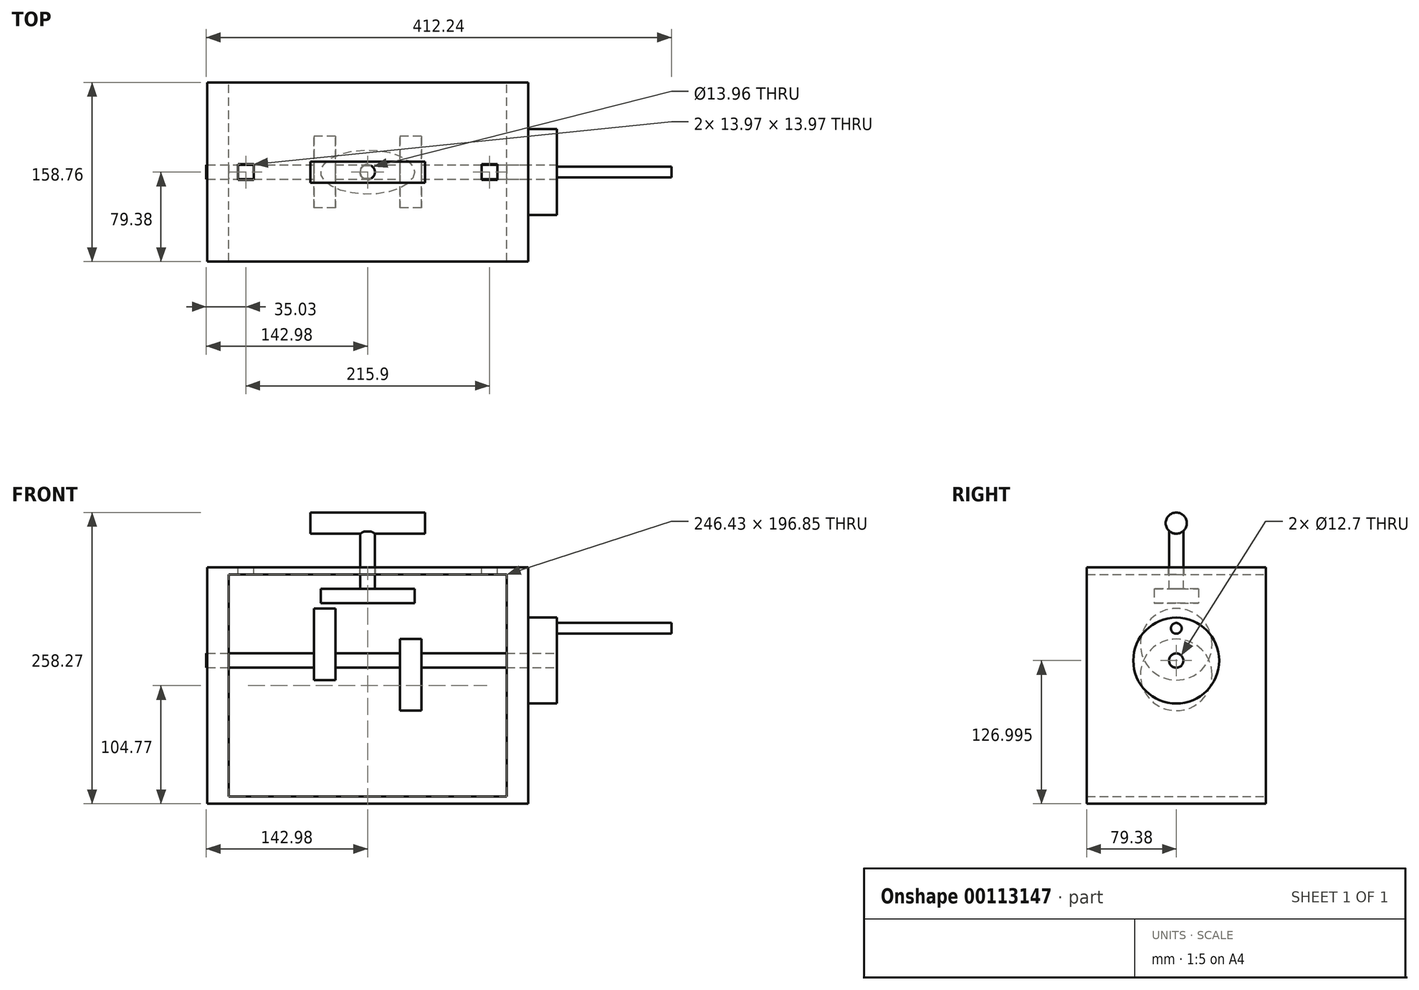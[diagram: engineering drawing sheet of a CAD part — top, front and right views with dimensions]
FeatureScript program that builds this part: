
annotation { "Feature Type Name" : "Feature", "Feature Type Description" : "" }
export const myFeature = defineFeature(function(context is Context, id is Id, definition is map)
    precondition{}
    {
        {
            var Q0;
            Q0=qCreatedBy(makeId("Front.planeOp"),FACE);
            var sketch = newSketch(context, id + "F0", { "sketchPlane" : qUnion([Q0])});
            skLineSegment(sketch, "E0.bottom", {"start": v(142.26, 104.78) * mm, "end": v(-142.26, 104.77) * mm});
            skLineSegment(sketch, "E0.top", {"start": v(142.26, -104.77) * mm, "end": v(-142.26, -104.78) * mm});
            skLineSegment(sketch, "E0.left", {"start": v(142.26, 104.78) * mm, "end": v(142.26, -104.77) * mm});
            skLineSegment(sketch, "E0.right", {"start": v(-142.26, 104.77) * mm, "end": v(-142.26, -104.78) * mm});
            skPoint(sketch, "E0.middle", {"position": v(0, 0) * mm});
            skLineSegment(sketch, "E1.bottom", {"start": v(123.21, 98.43) * mm, "end": v(-123.21, 98.42) * mm});
            skLineSegment(sketch, "E1.top", {"start": v(123.21, -98.43) * mm, "end": v(-123.21, -98.43) * mm});
            skLineSegment(sketch, "E1.left", {"start": v(123.21, 98.43) * mm, "end": v(123.21, -98.42) * mm});
            skLineSegment(sketch, "E1.right", {"start": v(-123.21, 98.42) * mm, "end": v(-123.21, -98.43) * mm});
            skSolve(sketch);
        }
        {
            var Q0;
            Q0 = qSketchRegion(id + "F0", true);
            extrude(context, id + "F1", {"entities" : qUnion([Q0]), "endBound" : BoundingType.SYMMETRIC, "depth" : 158.75 * mm});
        }
        {
            var Q0;
            Q0=makeQuery(id+"F1.opExtrude","SWEPT_FACE",FACE,{"disambiguationData":[OSD([sQuery(id+"F0.wireOp",EDGE,"E0.left")])]});
            var sketch = newSketch(context, id + "F2", { "sketchPlane" : qUnion([Q0])});
            skCircle(sketch, "E2", {"center": v(0, 22.22) * mm, "radius": 38.1 * mm});
            skSolve(sketch);
        }
        {
            var Q0;
            Q0=makeQuery(id+"F2.imprint","IMPRINT",FACE,{"disambiguationData":[TD([[makeQuery(id+"F2.imprint","IMPRINT",EDGE,{"derivedFrom":sQuery(id+"F2.wireOp",EDGE,"E2")}),1.0]])]});
            extrude(context, id + "F3", {"entities" : qUnion([Q0]), "depth" : 25.4 * mm});
        }
        {
            var Q0;
            Q0=makeQuery(id+"F3.opExtrude","CAP_FACE",FACE,{"disambiguationData":[OSD([sQuery(id+"F2.wireOp",EDGE,"E2")])],"isStart":false});
            var sketch = newSketch(context, id + "F4", { "sketchPlane" : qUnion([Q0])});
            skCircle(sketch, "E3", {"center": v(0, 50.8) * mm, "radius": 4.76 * mm});
            skLineSegment(sketch, "E4", {"start": v(0, 22.22) * mm, "end": v(0, 50.8) * mm, "construction": true});
            skSolve(sketch);
        }
        {
            var Q0;
            Q0 = qSketchRegion(id + "F4", true);
            extrude(context, id + "F5", {"entities" : qUnion([Q0]), "depth" : 101.6 * mm});
        }
        {
            var Q0;
            Q0=makeQuery(id+"F1.opExtrude","SWEPT_FACE",FACE,{"disambiguationData":[OSD([sQuery(id+"F0.wireOp",EDGE,"E0.left")])]});
            var sketch = newSketch(context, id + "F6", { "sketchPlane" : qUnion([Q0])});
            skCircle(sketch, "E5.0", {"center": v(0, 22.22) * mm, "radius": 38.1 * mm, "construction": true});
            skCircle(sketch, "E6", {"center": v(0, 22.22) * mm, "radius": 6.35 * mm});
            skSolve(sketch);
        }
        {
            var Q0;
            Q0 = qSketchRegion(id + "F6", true);
            extrude(context, id + "F7", {"entities" : qUnion([Q0]), "operationType" : NewBodyOperationType.REMOVE, "endBound" : BoundingType.THROUGH_ALL, "oppositeDirection" : true, "depth" : 25.4 * mm});
        }
        {
            var Q0;
            Q0=makeQuery(id+"F3.opExtrude","CAP_FACE",FACE,{"disambiguationData":[OSD([sQuery(id+"F2.wireOp",EDGE,"E2")])],"isStart":false});
            var sketch = newSketch(context, id + "F8", { "sketchPlane" : qUnion([Q0])});
            skCircle(sketch, "E7.0", {"center": v(0, 22.22) * mm, "radius": 6.35 * mm});
            skSolve(sketch);
        }
        {
            var Q0;
            Q0 = qSketchRegion(id + "F8", true);
            extrude(context, id + "F9", {"entities" : qUnion([Q0]), "oppositeDirection" : true, "depth" : 310.64 * mm});
        }
        {
            var Q0;
            Q0=makeQuery(id+"F1.opExtrude","SWEPT_FACE",FACE,{"disambiguationData":[OSD([sQuery(id+"F0.wireOp",EDGE,"E0.bottom")])]});
            var sketch = newSketch(context, id + "F10", { "sketchPlane" : qUnion([Q0])});
            skCircle(sketch, "E8", {"center": v(0, 0) * mm, "radius": 6.98 * mm});
            skSolve(sketch);
        }
        {
            var Q0;
            Q0 = qSketchRegion(id + "F10", true);
            extrude(context, id + "F11", {"entities" : qUnion([Q0]), "operationType" : NewBodyOperationType.REMOVE, "oppositeDirection" : true, "depth" : 25.4 * mm});
        }
        {
            var Q0;
            Q0=qCreatedBy(makeId("Right.planeOp"),FACE);
            cPlane(context, id + "F12", {"entities" : qUnion([Q0]), "cplaneType" : CPlaneType.OFFSET, "offset" : 38.1 * mm, "width" : 152.4 * mm, "height" : 152.4 * mm});
        }
        {
            var Q0;
            Q0=qCreatedBy(makeId("Right.planeOp"),FACE);
            cPlane(context, id + "F13", {"entities" : qUnion([Q0]), "cplaneType" : CPlaneType.OFFSET, "offset" : 38.1 * mm, "oppositeDirection" : true, "width" : 152.4 * mm, "height" : 152.4 * mm});
        }
        {
            var Q0;
            Q0=makeQuery(id+"F1.opExtrude","SWEPT_FACE",FACE,{"disambiguationData":[OSD([sQuery(id+"F0.wireOp",EDGE,"E0.bottom")])]});
            var sketch = newSketch(context, id + "F14", { "sketchPlane" : qUnion([Q0])});
            skCircle(sketch, "E9", {"center": v(0, 0) * mm, "radius": 6.45 * mm});
            skSolve(sketch);
        }
        {
            var Q0;
            Q0 = qSketchRegion(id + "F14", true);
            extrude(context, id + "F15", {"entities" : qUnion([Q0]), "endBound" : BoundingType.SYMMETRIC, "oppositeDirection" : true, "depth" : 63.5 * mm});
        }
        {
            var Q0;
            Q0=makeQuery(id+"F15.opExtrude","CAP_FACE",FACE,{"disambiguationData":[OSD([sQuery(id+"F14.wireOp",EDGE,"E9")])],"isStart":false});
            var sketch = newSketch(context, id + "F16", { "sketchPlane" : qUnion([Q0])});
            skEllipse(sketch, "E10", {"center": v(0, 0) * mm, "majorRadius": 41.54 * mm, "minorRadius": 19.6 * mm, "majorAxis": v(1, 0)});
            skSolve(sketch);
        }
        {
            var Q0;
            Q0=makeQuery(id+"F16.imprint","IMPRINT",FACE,{"disambiguationData":[TD([[makeQuery(id+"F16.imprint","IMPRINT",EDGE,{"derivedFrom":sQuery(id+"F16.wireOp",EDGE,"E10")}),1.0]])]});
            var Q1;
            Q1=sQuery(id+"F16.wireOp",EDGE,"E10");
            extrude(context, id + "F17", {"entities" : qUnion([Q0]), "operationType" : NewBodyOperationType.ADD, "surfaceEntities" : qUnion([Q1]), "oppositeDirection" : true, "depth" : 12.7 * mm});
        }
        {
            var Q0;
            Q0=qCreatedBy(id+"F12.planeOp",FACE);
            var sketch = newSketch(context, id + "F18", { "sketchPlane" : qUnion([Q0])});
            skCircle(sketch, "E11.0", {"center": v(0, 22.23) * mm, "radius": 6.35 * mm});
            skCircle(sketch, "E12", {"center": v(0, 9.53) * mm, "radius": 31.75 * mm});
            skSolve(sketch);
        }
        {
            var Q0;
            Q0 = qSketchRegion(id + "F18", true);
            extrude(context, id + "F19", {"entities" : qUnion([Q0]), "operationType" : NewBodyOperationType.ADD, "endBound" : BoundingType.SYMMETRIC, "depth" : 19.05 * mm});
        }
        {
            var Q0;
            Q0=qCreatedBy(id+"F13.planeOp",FACE);
            var sketch = newSketch(context, id + "F20", { "sketchPlane" : qUnion([Q0])});
            skCircle(sketch, "E13.0", {"center": v(0, 9.53) * mm, "radius": 31.75 * mm, "construction": true});
            skCircle(sketch, "E14.0", {"center": v(0, 22.23) * mm, "radius": 6.35 * mm});
            skCircle(sketch, "E15", {"center": v(0, 36.64) * mm, "radius": 31.75 * mm});
            skLineSegment(sketch, "E16", {"start": v(0, 4.9) * mm, "end": v(0, -22.22) * mm, "construction": true});
            skLineSegment(sketch, "E17", {"start": v(0, 41.28) * mm, "end": v(0, 68.4) * mm, "construction": true});
            skLineSegment(sketch, "E18", {"start": v(0, 36.64) * mm, "end": v(0, 41.28) * mm, "construction": true});
            skLineSegment(sketch, "E19", {"start": v(0, 9.53) * mm, "end": v(0, 4.9) * mm, "construction": true});
            skSolve(sketch);
        }
        {
            var Q0;
            Q0 = qSketchRegion(id + "F20", true);
            extrude(context, id + "F21", {"entities" : qUnion([Q0]), "operationType" : NewBodyOperationType.ADD, "endBound" : BoundingType.SYMMETRIC, "depth" : 19.05 * mm});
        }
        {
            var Q0;
            Q0=makeQuery(id+"F1.opExtrude","SWEPT_FACE",FACE,{"disambiguationData":[OSD([sQuery(id+"F0.wireOp",EDGE,"E0.bottom")])]});
            var sketch = newSketch(context, id + "F22", { "sketchPlane" : qUnion([Q0])});
            skLineSegment(sketch, "E20.bottom", {"start": v(-100.97, 6.99) * mm, "end": v(-114.94, 6.99) * mm});
            skLineSegment(sketch, "E20.top", {"start": v(-100.97, -6.98) * mm, "end": v(-114.94, -6.98) * mm});
            skLineSegment(sketch, "E20.left", {"start": v(-100.97, 6.99) * mm, "end": v(-100.97, -6.98) * mm});
            skLineSegment(sketch, "E20.right", {"start": v(-114.94, 6.99) * mm, "end": v(-114.94, -6.98) * mm});
            skPoint(sketch, "E20.middle", {"position": v(-107.95, 0) * mm});
            skLineSegment(sketch, "E21.bottom", {"start": v(114.94, 6.99) * mm, "end": v(100.96, 6.99) * mm});
            skLineSegment(sketch, "E21.top", {"start": v(114.94, -6.98) * mm, "end": v(100.96, -6.98) * mm});
            skLineSegment(sketch, "E21.left", {"start": v(114.93, 6.99) * mm, "end": v(114.93, -6.98) * mm});
            skLineSegment(sketch, "E21.right", {"start": v(100.96, 6.99) * mm, "end": v(100.96, -6.98) * mm});
            skPoint(sketch, "E21.middle", {"position": v(107.95, 0) * mm});
            skSolve(sketch);
        }
        {
            var Q0;
            Q0 = qSketchRegion(id + "F22", true);
            extrude(context, id + "F23", {"entities" : qUnion([Q0]), "operationType" : NewBodyOperationType.REMOVE, "oppositeDirection" : true, "depth" : 38.1 * mm});
        }
        {
            var Q0;
            Q0=qCreatedBy(makeId("Right.planeOp"),FACE);
            var sketch = newSketch(context, id + "F24", { "sketchPlane" : qUnion([Q0])});
            skCircle(sketch, "E22", {"center": v(0, 144.11) * mm, "radius": 9.39 * mm});
            skSolve(sketch);
        }
        {
            var Q0;
            Q0=makeQuery(id+"F24.imprint","IMPRINT",FACE,{"disambiguationData":[TD([[makeQuery(id+"F24.imprint","IMPRINT",EDGE,{"derivedFrom":sQuery(id+"F24.wireOp",EDGE,"E22")}),1.0]])]});
            var Q1;
            Q1=sQuery(id+"F24.wireOp",EDGE,"E22");
            extrude(context, id + "F25", {"entities" : qUnion([Q0]), "operationType" : NewBodyOperationType.ADD, "surfaceEntities" : qUnion([Q1]), "endBound" : BoundingType.SYMMETRIC, "depth" : 101.6 * mm});
        }
    });
